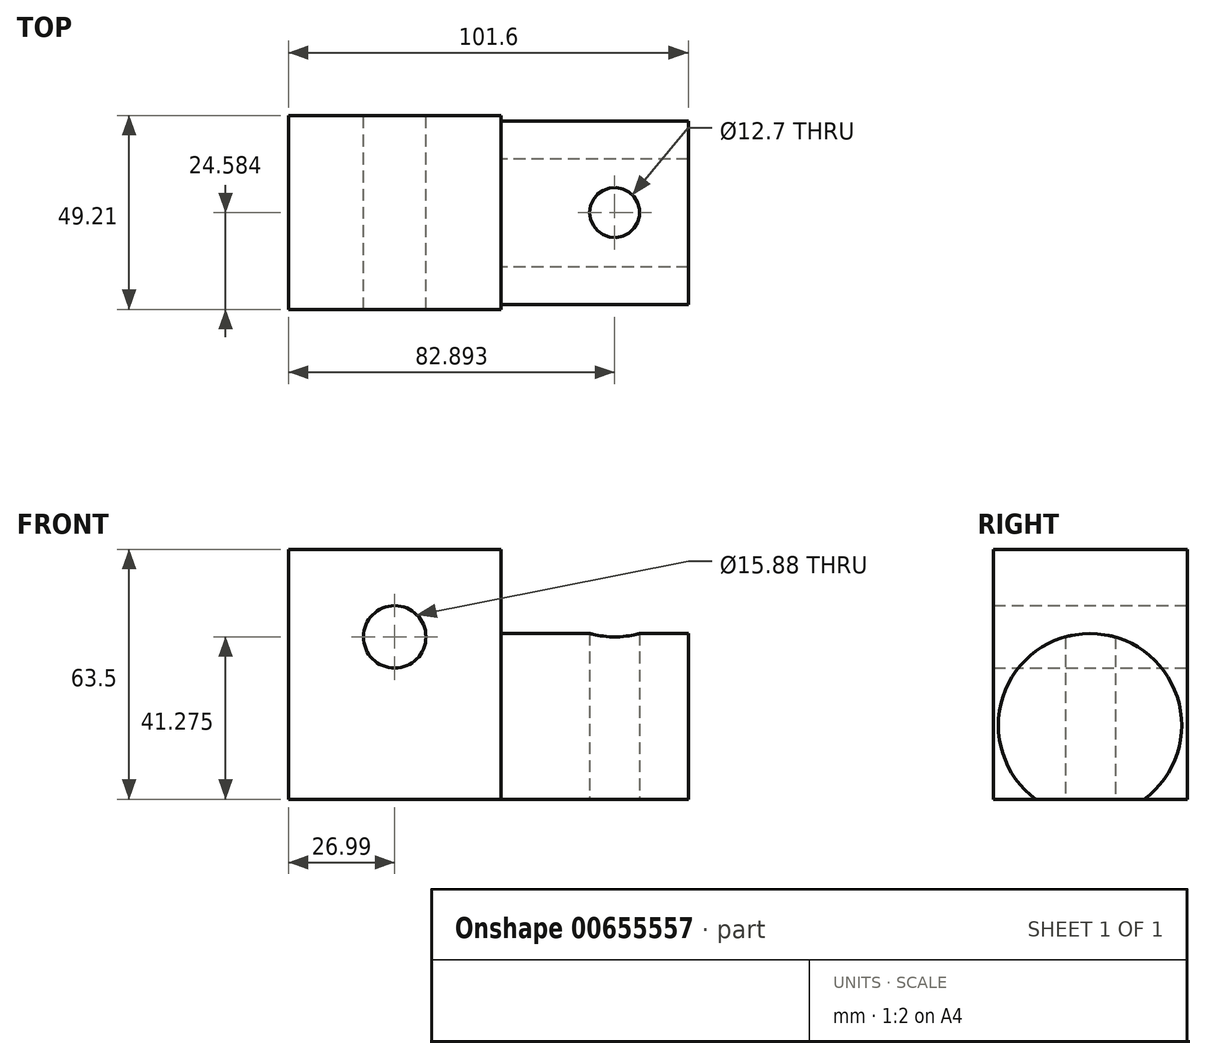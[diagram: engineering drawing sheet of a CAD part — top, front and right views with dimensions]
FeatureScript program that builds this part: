
annotation { "Feature Type Name" : "Feature", "Feature Type Description" : "" }
export const myFeature = defineFeature(function(context is Context, id is Id, definition is map)
    precondition{}
    {
        {
            var Q0;
            Q0=qCreatedBy(makeId("Front.planeOp"),FACE);
            var sketch = newSketch(context, id + "F0", { "sketchPlane" : qUnion([Q0])});
            skLineSegment(sketch, "E0.bottom", {"start": v(26.99, 31.75) * mm, "end": v(-26.99, 31.75) * mm});
            skLineSegment(sketch, "E0.top", {"start": v(26.99, -31.75) * mm, "end": v(-26.99, -31.75) * mm});
            skLineSegment(sketch, "E0.left", {"start": v(26.99, 31.75) * mm, "end": v(26.99, -31.75) * mm});
            skLineSegment(sketch, "E0.right", {"start": v(-26.99, 31.75) * mm, "end": v(-26.99, -31.75) * mm});
            skPoint(sketch, "E0.middle", {"position": v(0, 0) * mm});
            skCircle(sketch, "E1", {"center": v(0, 9.52) * mm, "radius": 7.94 * mm});
            skSolve(sketch);
        }
        {
            var Q0;
            Q0=makeQuery(id+"F0.imprint","IMPRINT",FACE,{"disambiguationData":[TD([[makeQuery(id+"F0.imprint","IMPRINT",EDGE,{"derivedFrom":sQuery(id+"F0.wireOp",EDGE,"E0.bottom")}),1.0]])]});
            extrude(context, id + "F1", {"entities" : qUnion([Q0]), "depth" : 49.2 * mm, "offsetDistance" : 25.4 * mm});
        }
        {
            var Q0;
            Q0=makeQuery(id+"F1.opExtrude","SWEPT_FACE",FACE,{"disambiguationData":[OSD([sQuery(id+"F0.wireOp",EDGE,"E0.left")])]});
            var sketch = newSketch(context, id + "F2", { "sketchPlane" : qUnion([Q0])});
            skArc(sketch, "E2", {"start": v(-11.01, -31.75) * mm, "mid": v(-24.73, 10.37) * mm, "end": v(-38.45, -31.75) * mm});
            skPoint(sketch, "E2.first.point", {"position": v(-37.82, 6.34) * mm});
            skPoint(sketch, "E2.second.point", {"position": v(-11.01, -31.75) * mm});
            skPoint(sketch, "E2.third.point", {"position": v(-38.45, -31.75) * mm});
            skLineSegment(sketch, "E3", {"start": v(-38.45, -31.75) * mm, "end": v(-11.01, -31.75) * mm});
            skLineSegment(sketch, "E4", {"start": v(-55.07, 10.08) * mm, "end": v(14.76, 10.08) * mm, "construction": true});
            skSolve(sketch);
        }
        {
            var Q0;
            Q0 = qSketchRegion(id + "F2", true);
            var Q1;
            Q1=makeQuery(id+"F2.imprint","IMPRINT",FACE,{"disambiguationData":[TD([[makeQuery(id+"F2.imprint","IMPRINT",EDGE,{"derivedFrom":sQuery(id+"F2.wireOp",EDGE,"E2")}),1.0]])]});
            extrude(context, id + "F3", {"entities" : qUnion([Q0, Q1]), "depth" : 47.62 * mm, "offsetDistance" : 25.4 * mm});
        }
        {
            var Q0;
            Q0=makeQuery(id+"F3.opExtrude","SWEPT_FACE",FACE,{"disambiguationData":[OSD([sQuery(id+"F2.wireOp",EDGE,"E3")])]});
            var sketch = newSketch(context, id + "F4", { "sketchPlane" : qUnion([Q0])});
            skPoint(sketch, "E5", {"position": v(55.9, 24.63) * mm});
            skSolve(sketch);
        }
        {
            var Q0;
            Q0=sQuery(id+"F4.wireOp",VERTEX,"E5");
            var Q1;
            Q1=makeQuery(id+"F3.opExtrude","SWEPT_BODY",BODY,{"disambiguationData":[OSD([sQuery(id+"F2.wireOp",EDGE,"E2"),sQuery(id+"F2.wireOp",EDGE,"E3")])]});
            hole(context, id + "F5", {"style" : HoleStyle.SIMPLE, "endStyle" : HoleEndStyle.BLIND, "holeDiameter" : 12.7 * mm, "majorDiameter" : 6.35 * mm, "holeDepth" : 50.8 * mm, "isTappedThrough" : true, "tappedDepth" : 12.7 * mm, "tapClearance" : 3, "startFromSketch" : true, "locations" : qUnion([Q0]), "scope" : qUnion([Q1])});
        }
    });
